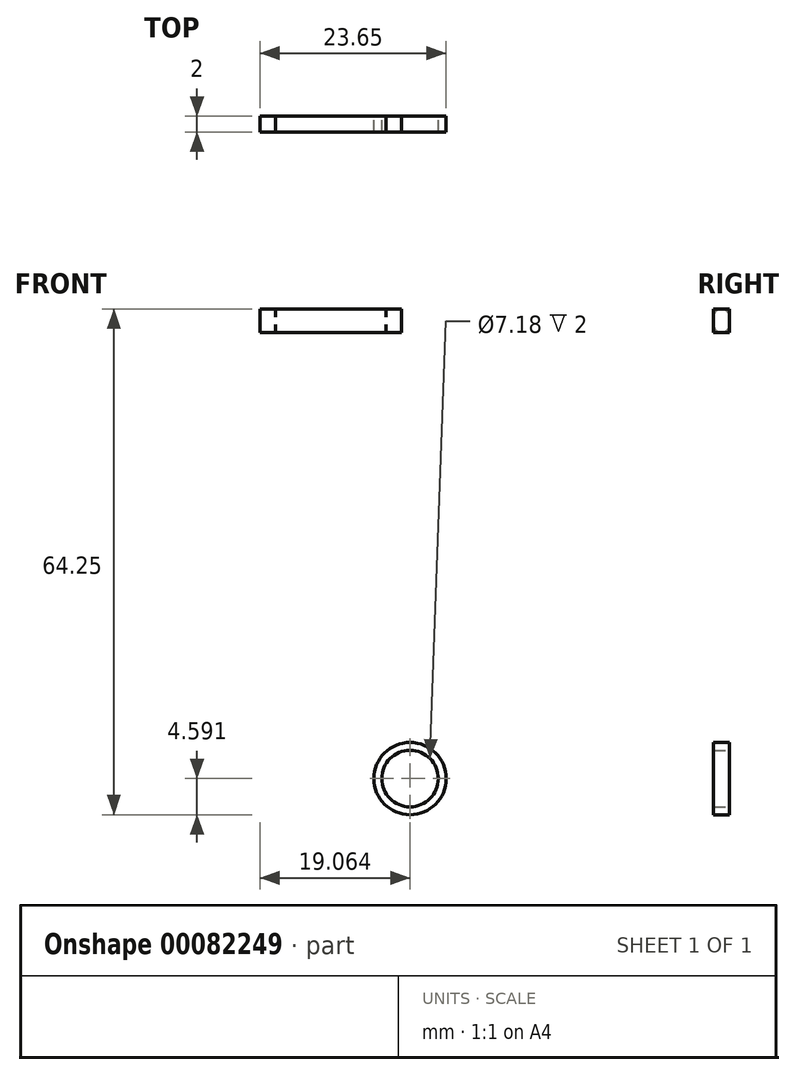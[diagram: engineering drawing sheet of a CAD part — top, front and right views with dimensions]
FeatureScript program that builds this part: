
annotation { "Feature Type Name" : "Feature", "Feature Type Description" : "" }
export const myFeature = defineFeature(function(context is Context, id is Id, definition is map)
    precondition{}
    {
        {
            var Q0;
            Q0=qCreatedBy(makeId("Front.planeOp"),FACE);
            var sketch = newSketch(context, id + "F0", { "sketchPlane" : qUnion([Q0])});
            skLineSegment(sketch, "E0", {"start": v(-43.36, 31.84) * mm, "end": v(-29.36, 31.84) * mm});
            skLineSegment(sketch, "E1", {"start": v(-43.36, 31.84) * mm, "end": v(-43.36, 28.84) * mm});
            skLineSegment(sketch, "E2", {"start": v(-43.36, 28.84) * mm, "end": v(-29.36, 28.84) * mm});
            skLineSegment(sketch, "E3", {"start": v(-29.36, 28.84) * mm, "end": v(-29.36, 31.84) * mm});
            skSolve(sketch);
        }
        {
            var Q0;
            Q0=makeQuery(id+"F0.imprint","IMPRINT",FACE,{"disambiguationData":[TD([[makeQuery(id+"F0.imprint","IMPRINT",EDGE,{"derivedFrom":sQuery(id+"F0.wireOp",EDGE,"E0")}),-1.0]])]});
            extrude(context, id + "F1", {"entities" : qUnion([Q0]), "depth" : 2 * mm});
        }
        {
            var Q0;
            Q0=makeQuery(id+"F1.opExtrude","SWEPT_FACE",FACE,{"disambiguationData":[OSD([sQuery(id+"F0.wireOp",EDGE,"E1")])]});
            var sketch = newSketch(context, id + "F2", { "sketchPlane" : qUnion([Q0])});
            skLineSegment(sketch, "E4", {"start": v(0, 31.84) * mm, "end": v(0, 28.84) * mm});
            skLineSegment(sketch, "E5", {"start": v(0, 28.84) * mm, "end": v(2, 28.84) * mm});
            skLineSegment(sketch, "E6", {"start": v(2, 28.84) * mm, "end": v(2, 31.84) * mm});
            skLineSegment(sketch, "E7", {"start": v(2, 31.84) * mm, "end": v(0, 31.84) * mm});
            skSolve(sketch);
        }
        {
            var Q0;
            Q0=makeQuery(id+"F1.opExtrude","SWEPT_FACE",FACE,{"disambiguationData":[OSD([sQuery(id+"F0.wireOp",EDGE,"E3")])]});
            var sketch = newSketch(context, id + "F3", { "sketchPlane" : qUnion([Q0])});
            skLineSegment(sketch, "E8", {"start": v(-2, 31.84) * mm, "end": v(-2, 28.84) * mm});
            skLineSegment(sketch, "E9", {"start": v(-2, 28.84) * mm, "end": v(0, 28.84) * mm});
            skLineSegment(sketch, "E10", {"start": v(0, 28.84) * mm, "end": v(0, 31.84) * mm});
            skLineSegment(sketch, "E11", {"start": v(0, 31.84) * mm, "end": v(-2, 31.84) * mm});
            skSolve(sketch);
        }
        {
            var Q0;
            Q0=makeQuery(id+"F1.opExtrude","CAP_EDGE",EDGE,{"disambiguationData":[OSD([sQuery(id+"F0.wireOp",EDGE,"E0")])],"isStart":true});
            var Q1;
            Q1=makeQuery(id+"F1.opExtrude","CAP_EDGE",EDGE,{"disambiguationData":[OSD([sQuery(id+"F0.wireOp",EDGE,"E2")])],"isStart":true});
            var Q2;
            Q2=makeQuery(id+"F1.opExtrude","CAP_EDGE",EDGE,{"disambiguationData":[OSD([sQuery(id+"F0.wireOp",EDGE,"E0")])],"isStart":false});
            var Q3;
            Q3=makeQuery(id+"F1.opExtrude","CAP_EDGE",EDGE,{"disambiguationData":[OSD([sQuery(id+"F0.wireOp",EDGE,"E2")])],"isStart":false});
            fillet(context, id + "F4", {"entities" : qUnion([Q0, Q1, Q2, Q3]), "radius" : 1 * mm, "tangentPropagation" : true, "allowEdgeOverflow" : false});
        }
        {
            var Q0;
            Q0=makeQuery(id+"F2.imprint","IMPRINT",FACE,{"disambiguationData":[TD([[makeQuery(id+"F2.imprint","IMPRINT",EDGE,{"derivedFrom":sQuery(id+"F2.wireOp",EDGE,"E4")}),1.0]])]});
            extrude(context, id + "F5", {"entities" : qUnion([Q0]), "operationType" : NewBodyOperationType.ADD, "depth" : 2 * mm});
        }
        {
            var Q0;
            Q0=makeQuery(id+"F3.imprint","IMPRINT",FACE,{"disambiguationData":[TD([[makeQuery(id+"F3.imprint","IMPRINT",EDGE,{"derivedFrom":sQuery(id+"F3.wireOp",EDGE,"E8")}),-1.0]])]});
            extrude(context, id + "F6", {"entities" : qUnion([Q0]), "operationType" : NewBodyOperationType.ADD, "depth" : 2 * mm});
        }
        {
            var Q0;
            Q0=qCreatedBy(makeId("Front.planeOp"),FACE);
            var sketch = newSketch(context, id + "F7", { "sketchPlane" : qUnion([Q0])});
            skCircle(sketch, "E12", {"center": v(-26.3, -27.82) * mm, "radius": 3.59 * mm});
            skCircle(sketch, "E13", {"center": v(-26.3, -27.82) * mm, "radius": 4.6 * mm});
            skSolve(sketch);
        }
        {
            var Q0;
            Q0 = qSketchRegion(id + "F7", true);
            extrude(context, id + "F8", {"entities" : qUnion([Q0]), "depth" : 2 * mm});
        }
    });
